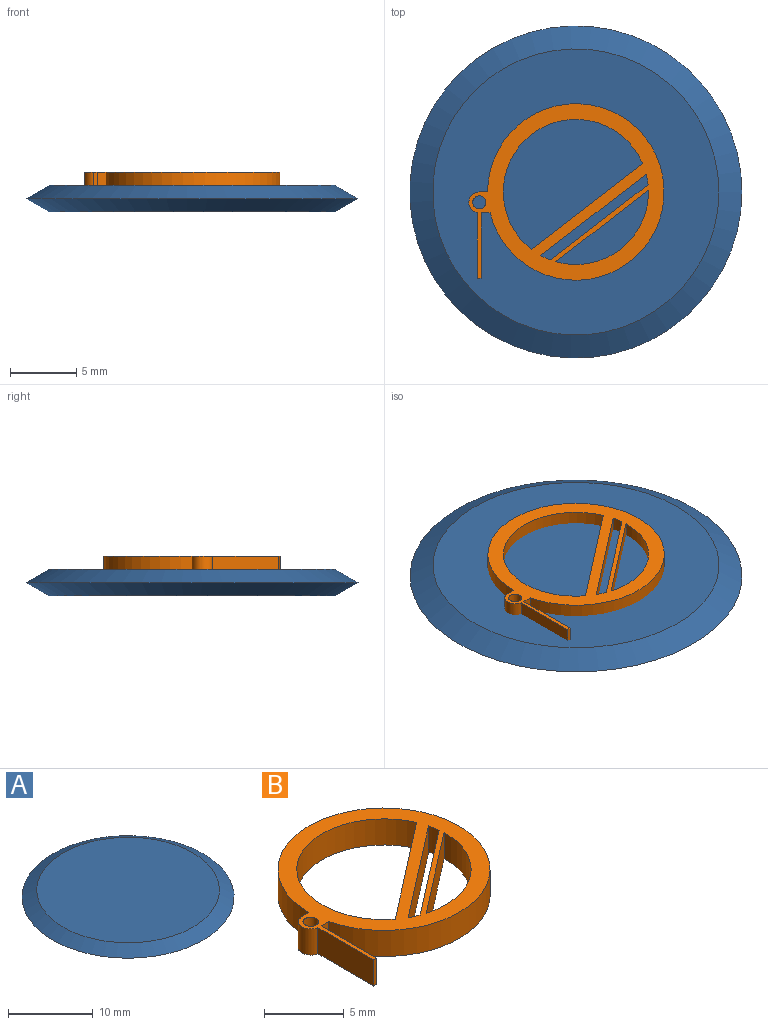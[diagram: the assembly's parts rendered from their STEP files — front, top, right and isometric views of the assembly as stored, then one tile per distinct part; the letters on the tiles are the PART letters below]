
ASSEMBLY  parts=2 mates=1
PART A: 4 faces, bbox 25x25x2 mm
  f0: plane 21.54x21.54mm, normal (0,0,1), area 364.3mm2, adj f1
  f1: cone r=12.5mm half-angle=60deg, axis (0,0,-1), area 146.2mm2, adj f0,f2
  f2: cone r=12.5mm half-angle=60deg, axis (0,0,1), area 146.2mm2, adj f1,f3
  f3: plane 21.54x21.54mm, normal (0,0,-1), area 364.3mm2, adj f2
PART B: 18 faces, bbox 14.7x13.3x2 mm
  f0: cylinder r=6.64mm len=13.29mm, axis (0,0,-1), area 80.3mm2, adj f1,f11,f16,f17
  f1: plane 2x0.68mm, normal (0,-1,0), area 1.4mm2, adj f0,f2,f16,f17
  f2: plane 4.93x2mm, normal (1,0,0), area 9.9mm2, adj f1,f3,f16,f17
  f3: plane 2x0.28mm, normal (0,-1,0), area 0.6mm2, adj f2,f4,f16,f17
  f4: plane 4.95x2mm, normal (-1,0,0), area 9.9mm2, adj f3,f5,f16,f17
  f5: cylinder r=0.79mm len=2mm, axis (0,0,-1), area 4.7mm2, adj f4,f11,f16,f17
  f6: plane 8.36x6.46mm, normal (-0.61,0.79,0), area 21.1mm2, adj f12,f16,f17
  f7: plane 7.34x5.67mm, normal (-0.61,0.79,0), area 18.6mm2, adj f8,f13,f16,f17
  f8: cylinder r=5.46mm len=2mm, axis (0,0,-1), area 1.6mm2, adj f7,f9,f16,f17
  f9: plane 7.93x6.13mm, normal (0.61,-0.79,0), area 20.1mm2, adj f8,f13,f16,f17
  f10: cylinder r=5.46mm len=6.98mm, axis (0,0,-1), area 20.5mm2, adj f14,f16,f17
  f11: plane 2x0.62mm, normal (0,1,0), area 1.2mm2, adj f0,f5,f16,f17
  f12: cylinder r=5.46mm len=10.49mm, axis (0,0,-1), area 39.9mm2, adj f6,f16,f17
  f13: cylinder r=5.46mm len=2mm, axis (0,0,-1), area 1.6mm2, adj f7,f9,f16,f17
  f14: plane 6.97x5.39mm, normal (0.61,-0.79,0), area 17.6mm2, adj f10,f16,f17
  f15: cylinder r=0.49mm len=2mm, axis (0,0,-1), area 6.1mm2, adj f16,f17
  f16: plane 14.7x13.29mm, normal (0,0,1), area 58.8mm2, adj f0,f1,f2,f3,f4,f5,f6,f7
  f17: plane 14.7x13.29mm, normal (0,0,-1), area 58.8mm2, adj f0,f1,f2,f3,f4,f5,f6,f7
PLACE A t=(-90.02,-0.12,-1.05)mm
PLACE B t=(-90.02,-0.12,-1.05)mm
MATE fastened A.f1 <-> B.f0  axis (0,0,1) through (-0.02,-0.12,-0.05)mm
